# Revit family: QF_COMCATER ALL BRANDS_RCF4
name_source: partatom
category: Specialty Equipment
revit_build: Autodesk Revit 2014 (Build: 20140709_2115(x64)
units: mm (PartAtom-declared; Revit-internal decimal feet)

## types (1)
- RCF4_Natural Gas
    Accessory = No
    Assembly Code = E1090320
    BTUH = 23800 W
    Depth Actual = 803 mm  [stored 2.63451 ft]
    Description = GAS DEEP FRYER
    Gas Flow = 0.0 L/s
    Gas Size = 19 mm
    Gas Size Flexible = 0 mm
    Gas power kW = 23.8
    Height Actual = 1235 mm
    Length Actual = 400 mm  [stored 1.31234 ft]
    Manufacturer = TRUEHEAT
    Model = RCF4
    Nominal Gas power = 23800 W
    Type Comments = The Australian owned and designed* Trueheat RC Series of Gas Cooking Equipment has been developed for the restaurant and cafe market with a high quality finish, designed to fulfill the busy demands within a commercial kitchen.
The RCF4 fryer is a high quality economical open pot design model. Its premium fast action thermostat allows for oil temperature to quickly recover.
It is durable and matches seamlessly with the Trueheat RC series.
It’s 18 litre capacity makes it ideal for small to medium sized restaurants, cafes and fast food outlets. It’s 100mj capacity combined with front mounted high quality thermostat produces 26kg of fries per hour. Stainless steel construction with premium higher grade stainless frypot. 1 1/4” drain.
Note: This fryer is not suitable for plinth mounting.

note: [stored X ft] marks values corroborated as IEEE doubles in the binary element streams (Revit-internal decimal feet)

## geometry (parser evidence)
native form markers: Sweep x6
no freeform markers — native parametric forms only
